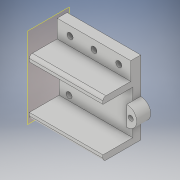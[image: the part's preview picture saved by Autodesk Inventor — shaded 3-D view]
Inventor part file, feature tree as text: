
AUTODESK INVENTOR PART (.ipt)
format: ipt  version: 2019 (Build 230136000, 136)  size: 335,360 bytes
history: native  units: mm
features: extrude x6, other x5, sketch x4, fillet x2, mirror x1, projected_geometry x1
ambient origin geometry x8: Origin, YZ Plane, XZ Plane, XY Plane, X Axis, Y Axis, Z Axis, Center Point
bodies: Body1 (feature_tree), Body2 (feature_tree)
feature tree (19):
  other  "Bryła1"
  sketch  "Szkic1"
  extrude  "Wyciągnięcie proste1"  Depth=37.0mm
  extrude  "Wyciągnięcie proste2"  Depth=22.0mm
  extrude  "Wyciągnięcie proste3"  Depth=5.0mm
  extrude  "Wyciągnięcie proste4"  Depth=2.5mm
  fillet  "Zaokrąglenie2"  Radius=3.0mm
  fillet  "Zaokrąglenie3"  Radius=3.0mm
  extrude  "Wyciągnięcie proste5"  Depth=37.0mm
  extrude  "Wyciągnięcie proste6"  Depth=3.0mm
  mirror  "Odbij1"
  other  "Płaszczyzna konstrukcyjna1"
  other  "Podział1"
  sketch  "Szkic2"
  sketch  "Szkic3"
  projected_geometry  "Pętla rzutowana1"
  sketch  "Szkic4"
  other  "Szyk z Bryła1:1"
  other  "Bryła2"
